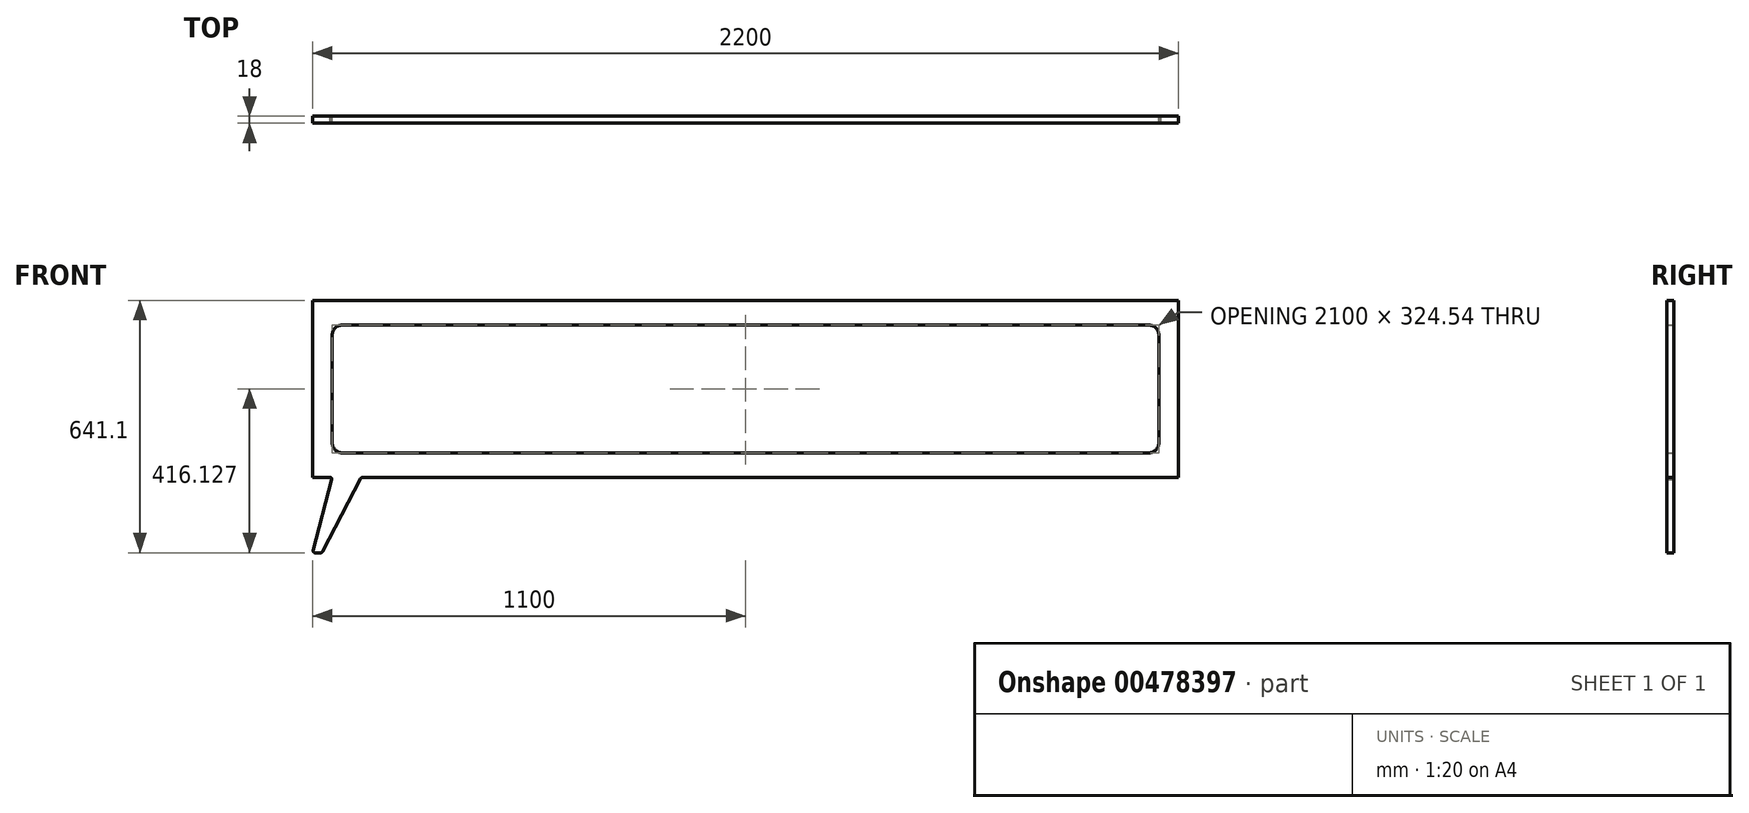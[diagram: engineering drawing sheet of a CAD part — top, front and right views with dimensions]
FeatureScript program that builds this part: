
annotation { "Feature Type Name" : "Feature", "Feature Type Description" : "" }
export const myFeature = defineFeature(function(context is Context, id is Id, definition is map)
    precondition{}
    {
        {
            var Q0;
            Q0=qCreatedBy(makeId("Front.planeOp"),FACE);
            var sketch = newSketch(context, id + "F0", { "sketchPlane" : qUnion([Q0])});
            skLineSegment(sketch, "E0.bottom", {"start": v(-1100, 75.88) * mm, "end": v(0, 75.88) * mm});
            skLineSegment(sketch, "E0.top", {"start": v(-1100, -374.12) * mm, "end": v(-1055, -374.12) * mm});
            skLineSegment(sketch, "E0.left", {"start": v(-1100, 75.88) * mm, "end": v(-1100, -374.12) * mm});
            skLineSegment(sketch, "E0.right", {"start": v(0, 4.02) * mm, "end": v(0, -324.06) * mm, "construction": true});
            skLineSegment(sketch, "E1", {"start": v(-1100, -374.12) * mm, "end": v(-1100, -565.22) * mm, "construction": true});
            skLineSegment(sketch, "E2", {"start": v(-1050, -374.12) * mm, "end": v(-1050, -374.12) * mm});
            skLineSegment(sketch, "E3", {"start": v(-1093.52, -565.22) * mm, "end": v(-1078.8, -565.22) * mm});
            skLineSegment(sketch, "E4", {"start": v(-1074.37, -562.53) * mm, "end": v(-977.78, -376.82) * mm});
            skLineSegment(sketch, "E5", {"start": v(-1050, -324.06) * mm, "end": v(-1050, -324.06) * mm});
            skPoint(sketch, "E6.visualSharp", {"position": v(-1100, -565.22) * mm});
            skArc(sketch, "E6.filletArc", {"start": v(-1098.36, -558.95) * mm, "mid": v(-1097.48, -563.28) * mm, "end": v(-1093.52, -565.22) * mm});
            skPoint(sketch, "E7.visualSharp", {"position": v(-1075.77, -565.22) * mm});
            skArc(sketch, "E7.filletArc", {"start": v(-1078.8, -565.22) * mm, "mid": v(-1076.21, -564.5) * mm, "end": v(-1074.37, -562.53) * mm});
            skLineSegment(sketch, "E8", {"start": v(-973.35, -374.12) * mm, "end": v(0, -374.12) * mm});
            skPoint(sketch, "E9.visualSharp", {"position": v(-976.38, -374.12) * mm});
            skArc(sketch, "E9.filletArc", {"start": v(-973.35, -374.12) * mm, "mid": v(-975.94, -374.85) * mm, "end": v(-977.78, -376.82) * mm});
            skArc(sketch, "E10", {"start": v(-1051.27, -378.96) * mm, "mid": v(-1051.86, -375.56) * mm, "end": v(-1055, -374.12) * mm});
            skLineSegment(sketch, "E11", {"start": v(-1051.27, -378.96) * mm, "end": v(-1098.36, -558.95) * mm});
            skArc(sketch, "E12.MirrorCS", {"start": v(1078.8, -565.22) * mm, "mid": v(1076.21, -564.5) * mm, "end": v(1074.37, -562.53) * mm});
            skLineSegment(sketch, "E13.MirrorCS", {"start": v(1093.52, -565.22) * mm, "end": v(1078.8, -565.22) * mm});
            skArc(sketch, "E14.MirrorCS", {"start": v(1098.36, -558.95) * mm, "mid": v(1097.48, -563.28) * mm, "end": v(1093.52, -565.22) * mm});
            skArc(sketch, "E15.MirrorCS", {"start": v(973.35, -374.12) * mm, "mid": v(975.94, -374.85) * mm, "end": v(977.78, -376.82) * mm});
            skArc(sketch, "E16.MirrorCS", {"start": v(1051.27, -378.96) * mm, "mid": v(1051.86, -375.56) * mm, "end": v(1055, -374.12) * mm});
            skPoint(sketch, "E17.MirrorP", {"position": v(1100, -565.22) * mm});
            skPoint(sketch, "E18.MirrorP", {"position": v(976.38, -374.12) * mm});
            skLineSegment(sketch, "E19.MirrorCS", {"start": v(1050, -374.12) * mm, "end": v(1050, -374.12) * mm});
            skLineSegment(sketch, "E20.MirrorCS", {"start": v(1074.37, -562.53) * mm, "end": v(977.78, -376.82) * mm});
            skLineSegment(sketch, "E21.MirrorCS", {"start": v(1100, 75.88) * mm, "end": v(1100, -374.12) * mm});
            skPoint(sketch, "E22.MirrorP", {"position": v(1075.77, -565.22) * mm});
            skLineSegment(sketch, "E23.MirrorCS", {"start": v(1100, -374.12) * mm, "end": v(1055, -374.12) * mm});
            skLineSegment(sketch, "E24.MirrorCS", {"start": v(1100, -374.12) * mm, "end": v(1100, -565.22) * mm, "construction": true});
            skLineSegment(sketch, "E25.MirrorCS", {"start": v(1051.27, -378.96) * mm, "end": v(1098.36, -558.95) * mm});
            skLineSegment(sketch, "E26.MirrorCS", {"start": v(1100, 75.88) * mm, "end": v(0, 75.88) * mm});
            skLineSegment(sketch, "E27.MirrorCS", {"start": v(973.35, -374.12) * mm, "end": v(0, -374.12) * mm});
            skPoint(sketch, "E28", {"position": v(0, 75.88) * mm});
            skPoint(sketch, "E29", {"position": v(0, 25.88) * mm});
            skLineSegment(sketch, "E30.left", {"start": v(-1050, -21.12) * mm, "end": v(-1050, -21.17) * mm});
            skPoint(sketch, "E31", {"position": v(-1100, 75.88) * mm});
            skLineSegment(sketch, "E32.0", {"start": v(-1100, 66.88) * mm, "end": v(0, 66.88) * mm});
            skLineSegment(sketch, "E33.0", {"start": v(-1091, 75.88) * mm, "end": v(-1091, -374.12) * mm});
            skLineSegment(sketch, "E34.0", {"start": v(-1100, -365.12) * mm, "end": v(0, -365.12) * mm});
            skLineSegment(sketch, "E35.MirrorCS", {"start": v(1100, 66.88) * mm, "end": v(0, 66.88) * mm});
            skLineSegment(sketch, "E36.MirrorCS", {"start": v(1091, -365.12) * mm, "end": v(0, -365.12) * mm});
            skLineSegment(sketch, "E37.MirrorCS", {"start": v(1091, 75.88) * mm, "end": v(1091, -365.04) * mm});
            skLineSegment(sketch, "E38", {"start": v(-1055, -374.12) * mm, "end": v(-973.35, -374.12) * mm});
            skLineSegment(sketch, "E39.MirrorCS", {"start": v(1055, -374.12) * mm, "end": v(973.35, -374.12) * mm});
            skLineSegment(sketch, "E40", {"start": v(1091, -365.04) * mm, "end": v(1091, -365.12) * mm});
            skPoint(sketch, "E41.end.orphan", {"position": v(1091, -374.12) * mm});
            skPoint(sketch, "E42.orphan", {"position": v(1100, -365.12) * mm});
            skLineSegment(sketch, "E43", {"start": v(973.35, -374.12) * mm, "end": v(973.35, -365.12) * mm, "construction": true});
            skLineSegment(sketch, "E44.trimOffspring", {"start": v(-1050, -324.06) * mm, "end": v(-1050, -324.12) * mm});
            skLineSegment(sketch, "E45.trimOffspring", {"start": v(-1050, -311.36) * mm, "end": v(1050, -311.36) * mm, "construction": true});
            skLineSegment(sketch, "E46", {"start": v(-1050, 13.18) * mm, "end": v(-1050, -324.12) * mm, "construction": true});
            skLineSegment(sketch, "E47", {"start": v(-1050, 4.02) * mm, "end": v(0, 4.02) * mm, "construction": true});
            skPoint(sketch, "E48.MirrorCS.end.orphan", {"position": v(1050, -289.83) * mm});
            skPoint(sketch, "E48.MirrorCS.start.orphan", {"position": v(1050, -21.12) * mm});
            skPoint(sketch, "E49.MirrorCS.start.orphan", {"position": v(1026.76, -311.36) * mm});
            skPoint(sketch, "E50.MirrorCS.end.orphan", {"position": v(0, -311.36) * mm});
            skLineSegment(sketch, "E51.MirrorCS", {"start": v(1050, 27.4) * mm, "end": v(1050, -324.72) * mm, "construction": true});
            skPoint(sketch, "E52.orphan", {"position": v(-1025, 4.02) * mm});
            skPoint(sketch, "E53.orphan", {"position": v(-1050, -289.83) * mm});
            skPoint(sketch, "E54.orphan", {"position": v(-1026.76, -311.36) * mm});
            skLineSegment(sketch, "E55.top", {"start": v(-1025, -311.36) * mm, "end": v(1025, -311.36) * mm});
            skLineSegment(sketch, "E55.left", {"start": v(-1050, -11.82) * mm, "end": v(-1050, -286.36) * mm});
            skLineSegment(sketch, "E55.right", {"start": v(1050, -11.82) * mm, "end": v(1050, -286.36) * mm});
            skPoint(sketch, "E56.visualSharp", {"position": v(-1050, 4.02) * mm});
            skPoint(sketch, "E57.visualSharp", {"position": v(-1050, -311.36) * mm});
            skArc(sketch, "E57.filletArc", {"start": v(-1050, -286.36) * mm, "mid": v(-1042.68, -304.04) * mm, "end": v(-1025, -311.36) * mm});
            skPoint(sketch, "E58.visualSharp", {"position": v(1050, 4.02) * mm});
            skPoint(sketch, "E59.visualSharp", {"position": v(1050, -311.36) * mm});
            skArc(sketch, "E59.filletArc", {"start": v(1025, -311.36) * mm, "mid": v(1042.68, -304.04) * mm, "end": v(1050, -286.36) * mm});
            skLineSegment(sketch, "E60.0", {"start": v(-1025, 13.18) * mm, "end": v(1025, 13.18) * mm});
            skPoint(sketch, "E61.visualSharp", {"position": v(-1050, 13.18) * mm});
            skArc(sketch, "E61.filletArc", {"start": v(-1025, 13.18) * mm, "mid": v(-1042.68, 5.85) * mm, "end": v(-1050, -11.82) * mm});
            skPoint(sketch, "E62.visualSharp", {"position": v(1050, 13.18) * mm});
            skArc(sketch, "E62.filletArc", {"start": v(1050, -11.82) * mm, "mid": v(1042.68, 5.85) * mm, "end": v(1025, 13.18) * mm});
            skSolve(sketch);
        }
        {
            var Q0;
            {var subQ0=sQuery(id+"F0.wireOp",EDGE,"E0.left");var subQ1=sQuery(id+"F0.wireOp",EDGE,"E0.bottom");var subQ2=makeQuery(id+"F0.imprint","INTERSECT",VERTEX,{"derivedFrom":[subQ1,subQ0]});Q0=makeQuery(id+"F0.imprint","IMPRINT",FACE,{"disambiguationData":[TD([[makeQuery(id+"F0.imprint","IMPRINT",EDGE,{"disambiguationData":[TD([[subQ2,-1.0]])],"derivedFrom":subQ1}),-1.0]])]});}
            var Q1;
            Q1=makeQuery(id+"F0.imprint","IMPRINT",FACE,{"disambiguationData":[TD([[makeQuery(id+"F0.imprint","IMPRINT",EDGE,{"derivedFrom":sQuery(id+"F0.wireOp",EDGE,"E30.bottom")}),1.0]])]});
            var Q2;
            Q2=makeQuery(id+"F0.imprint","IMPRINT",FACE,{"disambiguationData":[TD([[makeQuery(id+"F0.imprint","IMPRINT",EDGE,{"derivedFrom":sQuery(id+"F0.wireOp",EDGE,"E3")}),1.0]])]});
            var Q3;
            {var subQ0=sQuery(id+"F0.wireOp",EDGE,"E35.MirrorCS");var subQ1=sQuery(id+"F0.wireOp",EDGE,"E21.MirrorCS");var subQ2=makeQuery(id+"F0.imprint","INTERSECT",VERTEX,{"derivedFrom":[subQ1,subQ0]});Q3=makeQuery(id+"F0.imprint","IMPRINT",FACE,{"disambiguationData":[TD([[makeQuery(id+"F0.imprint","IMPRINT",EDGE,{"disambiguationData":[TD([[subQ2,-1.0]])],"derivedFrom":subQ1}),-1.0]])]});}
            var Q4;
            {var subQ1=sQuery(id+"F0.wireOp",EDGE,"E0.bottom");var subQ7=sQuery(id+"F0.wireOp",EDGE,"E26.MirrorCS");var subQ8=makeQuery(id+"F0.imprint","INTERSECT",VERTEX,{"derivedFrom":[subQ1,subQ7]});Q4=makeQuery(id+"F0.imprint","IMPRINT",FACE,{"disambiguationData":[TD([[makeQuery(id+"F0.imprint","IMPRINT",EDGE,{"disambiguationData":[TD([[subQ8,1.0]])],"derivedFrom":subQ1}),-1.0]])]});}
            var Q5;
            {var subQ0=sQuery(id+"F0.wireOp",EDGE,"E32.0");var subQ1=sQuery(id+"F0.wireOp",EDGE,"E0.left");var subQ2=makeQuery(id+"F0.imprint","INTERSECT",VERTEX,{"derivedFrom":[subQ1,subQ0]});Q5=makeQuery(id+"F0.imprint","IMPRINT",FACE,{"disambiguationData":[TD([[makeQuery(id+"F0.imprint","IMPRINT",EDGE,{"disambiguationData":[TD([[subQ2,-1.0]])],"derivedFrom":subQ1}),1.0]])]});}
            var Q6;
            {var subQ0=sQuery(id+"F0.wireOp",EDGE,"E0.left");var subQ1=sQuery(id+"F0.wireOp",EDGE,"E0.top");var subQ2=makeQuery(id+"F0.imprint","INTERSECT",VERTEX,{"derivedFrom":[subQ1,subQ0]});Q6=makeQuery(id+"F0.imprint","IMPRINT",FACE,{"disambiguationData":[TD([[makeQuery(id+"F0.imprint","IMPRINT",EDGE,{"disambiguationData":[TD([[subQ2,-1.0]])],"derivedFrom":subQ1}),1.0]])]});}
            var Q7;
            {var subQ0=sQuery(id+"F0.wireOp",EDGE,"E21.MirrorCS");var subQ1=sQuery(id+"F0.wireOp",EDGE,"E26.MirrorCS");var subQ2=makeQuery(id+"F0.imprint","INTERSECT",VERTEX,{"derivedFrom":[subQ1,subQ0]});Q7=makeQuery(id+"F0.imprint","IMPRINT",FACE,{"disambiguationData":[TD([[makeQuery(id+"F0.imprint","IMPRINT",EDGE,{"disambiguationData":[TD([[subQ2,-1.0]])],"derivedFrom":subQ1}),1.0]])]});}
            var Q8;
            {var subQ0=sQuery(id+"F0.wireOp",EDGE,"E23.MirrorCS");var subQ1=sQuery(id+"F0.wireOp",EDGE,"E21.MirrorCS");var subQ2=makeQuery(id+"F0.imprint","INTERSECT",VERTEX,{"derivedFrom":[subQ1,subQ0]});Q8=makeQuery(id+"F0.imprint","IMPRINT",FACE,{"disambiguationData":[TD([[makeQuery(id+"F0.imprint","IMPRINT",EDGE,{"disambiguationData":[TD([[subQ2,1.0]])],"derivedFrom":subQ1}),-1.0]])]});}
            var Q9;
            Q9=makeQuery(id+"F0.imprint","IMPRINT",FACE,{"disambiguationData":[TD([[makeQuery(id+"F0.imprint","IMPRINT",EDGE,{"derivedFrom":sQuery(id+"F0.wireOp",EDGE,"E12.MirrorCS")}),-1.0]])]});
            var Q10;
            {var subQ10=sQuery(id+"F0.wireOp",EDGE,"E30.left");Q10=makeQuery(id+"F0.imprint","IMPRINT",FACE,{"disambiguationData":[TD([[makeQuery(id+"F0.imprint","IMPRINT",EDGE,{"derivedFrom":subQ10}),-1.0]])]});}
            var Q11;
            {var subQ4=sQuery(id+"F0.wireOp",EDGE,"E36.MirrorCS");Q11=makeQuery(id+"F0.imprint","IMPRINT",FACE,{"disambiguationData":[TD([[makeQuery(id+"F0.imprint","IMPRINT",EDGE,{"derivedFrom":subQ4}),-1.0]])]});}
            extrude(context, id + "F1", {"entities" : qUnion([Q0, Q1, Q2, Q3, Q4, Q5, Q6, Q7, Q8, Q9, Q10, Q11]), "depth" : 18 * mm});
        }
    });
